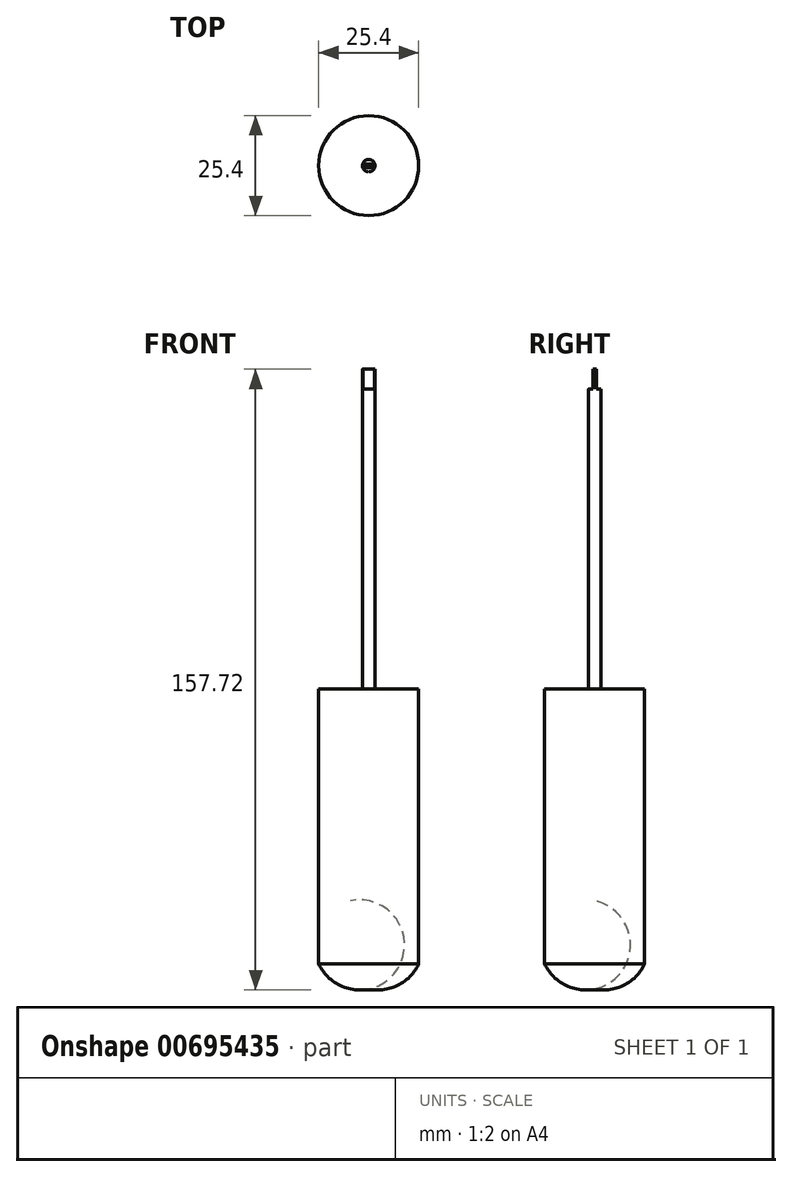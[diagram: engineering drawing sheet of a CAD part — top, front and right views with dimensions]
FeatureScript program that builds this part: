
annotation { "Feature Type Name" : "Feature", "Feature Type Description" : "" }
export const myFeature = defineFeature(function(context is Context, id is Id, definition is map)
    precondition{}
    {
        {
            var Q0;
            Q0=qCreatedBy(makeId("Front.planeOp"),FACE);
            var sketch = newSketch(context, id + "F0", { "sketchPlane" : qUnion([Q0])});
            skLineSegment(sketch, "E0", {"start": v(0, 0) * mm, "end": v(0, 76.2) * mm});
            skLineSegment(sketch, "E1", {"start": v(0, 76.2) * mm, "end": v(12.7, 76.2) * mm});
            skLineSegment(sketch, "E2", {"start": v(12.7, 76.2) * mm, "end": v(12.7, 6.35) * mm});
            skArc(sketch, "E3", {"start": v(0, 0) * mm, "mid": v(7.46, 0.96) * mm, "end": v(12.7, 6.35) * mm});
            skSolve(sketch);
        }
        {
            var Q0;
            Q0 = qSketchRegion(id + "F0", true);
            var Q1;
            Q1=sQuery(id+"F0.wireOp",EDGE,"E0");
            revolve(context, id + "F1", {"entities" : qUnion([Q0]), "axis" : qUnion([Q1]), "revolveType" : RevolveType.FULL});
        }
        {
            var Q0;
            Q0=qCreatedBy(makeId("Top.planeOp"),FACE);
            var sketch = newSketch(context, id + "F2", { "sketchPlane" : qUnion([Q0])});
            skCircle(sketch, "E4", {"center": v(0, 0) * mm, "radius": 1.59 * mm});
            skSolve(sketch);
        }
        {
            var Q0;
            Q0 = qSketchRegion(id + "F2", true);
            extrude(context, id + "F3", {"entities" : qUnion([Q0]), "operationType" : NewBodyOperationType.ADD, "depth" : 152.4 * mm, "offsetDistance" : 25.4 * mm});
        }
        {
            var Q0;
            Q0=makeQuery(id+"F3.opExtrude","CAP_FACE",FACE,{"disambiguationData":[OSD([sQuery(id+"F2.wireOp",EDGE,"E4")])],"isStart":false});
            var sketch = newSketch(context, id + "F4", { "sketchPlane" : qUnion([Q0])});
            skLineSegment(sketch, "E5", {"start": v(-1.52, 0.44) * mm, "end": v(1.52, 0.44) * mm});
            skLineSegment(sketch, "E6", {"start": v(-1.51, -0.49) * mm, "end": v(1.51, -0.49) * mm});
            skSolve(sketch);
        }
        {
            var Q0;
            {var subQ0=sQuery(id+"F4.wireOp",EDGE,"E5");Q0=makeQuery(id+"F4.imprint","IMPRINT",FACE,{"disambiguationData":[TD([[makeQuery(id+"F4.imprint","IMPRINT",EDGE,{"derivedFrom":subQ0}),-1.0]])]});}
            extrude(context, id + "F5", {"entities" : qUnion([Q0]), "operationType" : NewBodyOperationType.ADD, "depth" : 5.08 * mm, "offsetDistance" : 25.4 * mm});
        }
    });
